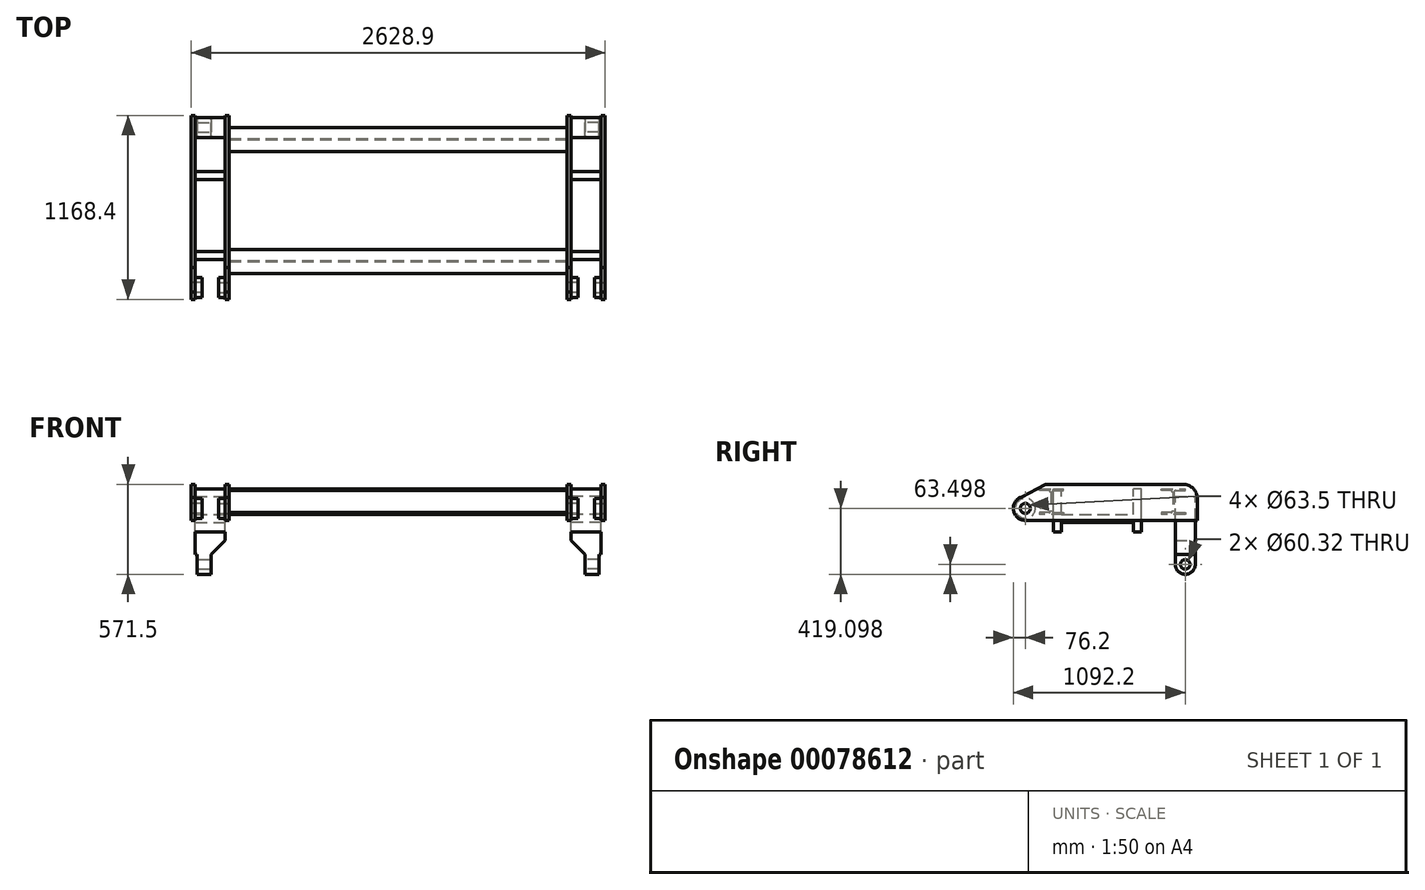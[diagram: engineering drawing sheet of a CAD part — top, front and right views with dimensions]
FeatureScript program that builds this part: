
annotation { "Feature Type Name" : "Feature", "Feature Type Description" : "" }
export const myFeature = defineFeature(function(context is Context, id is Id, definition is map)
    precondition{}
    {
        {
            var Q0;
            Q0=qCreatedBy(makeId("Right.planeOp"),FACE);
            var sketch = newSketch(context, id + "F0", { "sketchPlane" : qUnion([Q0])});
            skLineSegment(sketch, "E0", {"start": v(0, 94.66) * mm, "end": v(0, -108.5) * mm, "construction": true});
            skLineSegment(sketch, "E1.0", {"start": v(387.35, 94.66) * mm, "end": v(387.35, -76.51) * mm, "construction": true});
            skLineSegment(sketch, "E2", {"start": v(387.35, -6.92) * mm, "end": v(515.37, -6.92) * mm, "construction": true});
            skLineSegment(sketch, "E3.0", {"start": v(391.16, 49.98) * mm, "end": v(391.16, -63.81) * mm});
            skLineSegment(sketch, "E4.0", {"start": v(387.35, -87.94) * mm, "end": v(463.55, -87.94) * mm});
            skLineSegment(sketch, "E5.0", {"start": v(403.86, -76.51) * mm, "end": v(463.55, -76.51) * mm});
            skLineSegment(sketch, "E6.trimOffspring", {"start": v(463.55, -76.51) * mm, "end": v(463.55, -87.94) * mm});
            skLineSegment(sketch, "E7.0.MirrorCS", {"start": v(463.55, 62.68) * mm, "end": v(463.55, 74.11) * mm});
            skLineSegment(sketch, "E7.1.MirrorCS", {"start": v(387.35, 74.11) * mm, "end": v(463.55, 74.11) * mm});
            skLineSegment(sketch, "E7.2.MirrorCS", {"start": v(403.86, 62.68) * mm, "end": v(463.55, 62.68) * mm});
            skPoint(sketch, "E8.trimOffspring.end.orphan", {"position": v(387.35, -108.5) * mm});
            skLineSegment(sketch, "E9.0.MirrorCS", {"start": v(311.15, 62.68) * mm, "end": v(311.15, 74.11) * mm});
            skLineSegment(sketch, "E9.1.MirrorCS", {"start": v(311.15, -76.51) * mm, "end": v(311.15, -87.94) * mm});
            skLineSegment(sketch, "E9.2.MirrorCS", {"start": v(387.35, -87.94) * mm, "end": v(311.15, -87.94) * mm});
            skLineSegment(sketch, "E9.3.MirrorCS", {"start": v(383.54, 49.98) * mm, "end": v(383.54, -63.81) * mm});
            skLineSegment(sketch, "E9.4.MirrorCS", {"start": v(387.35, 74.11) * mm, "end": v(311.15, 74.11) * mm});
            skLineSegment(sketch, "E9.5.MirrorCS", {"start": v(370.84, 62.68) * mm, "end": v(311.15, 62.68) * mm});
            skLineSegment(sketch, "E9.6.MirrorCS", {"start": v(370.84, -76.51) * mm, "end": v(311.15, -76.51) * mm});
            skPoint(sketch, "E10.visualSharp", {"position": v(383.54, 62.68) * mm});
            skArc(sketch, "E10.filletArc", {"start": v(383.54, 49.98) * mm, "mid": v(379.82, 58.96) * mm, "end": v(370.84, 62.68) * mm});
            skPoint(sketch, "E11.visualSharp", {"position": v(391.16, 62.68) * mm});
            skArc(sketch, "E11.filletArc", {"start": v(403.86, 62.68) * mm, "mid": v(394.88, 58.96) * mm, "end": v(391.16, 49.98) * mm});
            skPoint(sketch, "E12.visualSharp", {"position": v(383.54, -76.51) * mm});
            skArc(sketch, "E12.filletArc", {"start": v(370.84, -76.51) * mm, "mid": v(379.82, -72.8) * mm, "end": v(383.54, -63.81) * mm});
            skPoint(sketch, "E13.visualSharp", {"position": v(391.16, -76.51) * mm});
            skArc(sketch, "E13.filletArc", {"start": v(391.16, -63.81) * mm, "mid": v(394.88, -72.8) * mm, "end": v(403.86, -76.51) * mm});
            skArc(sketch, "E14.0.MirrorCS", {"start": v(-403.86, 62.68) * mm, "mid": v(-394.88, 58.96) * mm, "end": v(-391.16, 49.98) * mm});
            skArc(sketch, "E14.1.MirrorCS", {"start": v(-391.16, -63.81) * mm, "mid": v(-394.88, -72.8) * mm, "end": v(-403.86, -76.51) * mm});
            skLineSegment(sketch, "E14.2.MirrorCS", {"start": v(-311.15, 62.68) * mm, "end": v(-311.15, 74.11) * mm});
            skArc(sketch, "E14.3.MirrorCS", {"start": v(-383.54, 49.98) * mm, "mid": v(-379.82, 58.96) * mm, "end": v(-370.84, 62.68) * mm});
            skArc(sketch, "E14.4.MirrorCS", {"start": v(-370.84, -76.51) * mm, "mid": v(-379.82, -72.8) * mm, "end": v(-383.54, -63.81) * mm});
            skLineSegment(sketch, "E14.5.MirrorCS", {"start": v(-311.15, -76.51) * mm, "end": v(-311.15, -87.94) * mm});
            skLineSegment(sketch, "E14.6.MirrorCS", {"start": v(-463.55, 62.68) * mm, "end": v(-463.55, 74.11) * mm});
            skLineSegment(sketch, "E14.7.MirrorCS", {"start": v(-463.55, -76.51) * mm, "end": v(-463.55, -87.94) * mm});
            skLineSegment(sketch, "E14.8.MirrorCS", {"start": v(-387.35, 94.66) * mm, "end": v(-387.35, -76.51) * mm, "construction": true});
            skPoint(sketch, "E14.9.MirrorP", {"position": v(-391.16, -76.51) * mm});
            skLineSegment(sketch, "E14.10.MirrorCS", {"start": v(-370.84, -76.51) * mm, "end": v(-311.15, -76.51) * mm});
            skPoint(sketch, "E14.11.MirrorP", {"position": v(-387.35, -108.5) * mm});
            skLineSegment(sketch, "E14.12.MirrorCS", {"start": v(-383.54, 49.98) * mm, "end": v(-383.54, -63.81) * mm});
            skPoint(sketch, "E14.13.MirrorP", {"position": v(-391.16, 62.68) * mm});
            skLineSegment(sketch, "E14.14.MirrorCS", {"start": v(-403.86, 62.68) * mm, "end": v(-463.55, 62.68) * mm});
            skLineSegment(sketch, "E14.15.MirrorCS", {"start": v(-403.86, -76.51) * mm, "end": v(-463.55, -76.51) * mm});
            skLineSegment(sketch, "E14.16.MirrorCS", {"start": v(-370.84, 62.68) * mm, "end": v(-311.15, 62.68) * mm});
            skLineSegment(sketch, "E14.17.MirrorCS", {"start": v(-387.35, 74.11) * mm, "end": v(-463.55, 74.11) * mm});
            skLineSegment(sketch, "E14.18.MirrorCS", {"start": v(-387.35, 74.11) * mm, "end": v(-311.15, 74.11) * mm});
            skPoint(sketch, "E14.19.MirrorP", {"position": v(-383.54, -76.51) * mm});
            skLineSegment(sketch, "E14.20.MirrorCS", {"start": v(-387.35, -87.94) * mm, "end": v(-463.55, -87.94) * mm});
            skPoint(sketch, "E14.21.MirrorP", {"position": v(-383.54, 62.68) * mm});
            skLineSegment(sketch, "E14.22.MirrorCS", {"start": v(-387.35, -87.94) * mm, "end": v(-311.15, -87.94) * mm});
            skLineSegment(sketch, "E14.23.MirrorCS", {"start": v(-391.16, 49.98) * mm, "end": v(-391.16, -63.81) * mm});
            skSolve(sketch);
        }
        {
            var Q0;
            Q0=qSketchRegion(id+"F0",true);
            extrude(context, id + "F1", {"entities" : qUnion([Q0]), "endBound" : BoundingType.SYMMETRIC, "depth" : 2146.3 * mm});
        }
        {
            var Q0;
            Q0=makeQuery(id+"F1.opExtrude","CAP_FACE",FACE,{"disambiguationData":[OSD([sQuery(id+"F0.wireOp",EDGE,"E14.0.MirrorCS"),sQuery(id+"F0.wireOp",EDGE,"E14.1.MirrorCS"),sQuery(id+"F0.wireOp",EDGE,"E14.2.MirrorCS"),sQuery(id+"F0.wireOp",EDGE,"E14.3.MirrorCS"),sQuery(id+"F0.wireOp",EDGE,"E14.4.MirrorCS"),sQuery(id+"F0.wireOp",EDGE,"E14.5.MirrorCS"),sQuery(id+"F0.wireOp",EDGE,"E14.6.MirrorCS"),sQuery(id+"F0.wireOp",EDGE,"E14.7.MirrorCS"),sQuery(id+"F0.wireOp",EDGE,"E14.10.MirrorCS"),sQuery(id+"F0.wireOp",EDGE,"E14.12.MirrorCS"),sQuery(id+"F0.wireOp",EDGE,"E14.14.MirrorCS"),sQuery(id+"F0.wireOp",EDGE,"E14.15.MirrorCS"),sQuery(id+"F0.wireOp",EDGE,"E14.16.MirrorCS"),sQuery(id+"F0.wireOp",EDGE,"E14.17.MirrorCS"),sQuery(id+"F0.wireOp",EDGE,"E14.18.MirrorCS"),sQuery(id+"F0.wireOp",EDGE,"E14.20.MirrorCS"),sQuery(id+"F0.wireOp",EDGE,"E14.22.MirrorCS"),sQuery(id+"F0.wireOp",EDGE,"E14.23.MirrorCS")])],"isStart":false});
            var sketch = newSketch(context, id + "F2", { "sketchPlane" : qUnion([Q0])});
            skLineSegment(sketch, "E15.0", {"start": v(311.15, 74.11) * mm, "end": v(463.55, 74.11) * mm, "construction": true});
            skLineSegment(sketch, "E16", {"start": v(387.35, 74.11) * mm, "end": v(387.35, -187.68) * mm, "construction": true});
            skLineSegment(sketch, "E17", {"start": v(539.75, 13.66) * mm, "end": v(539.75, -126.04) * mm});
            skLineSegment(sketch, "E18.0", {"start": v(450.85, 102.56) * mm, "end": v(-425.45, 102.56) * mm});
            skPoint(sketch, "E19.visualSharp", {"position": v(539.75, 102.56) * mm});
            skArc(sketch, "E19.filletArc", {"start": v(539.75, 13.66) * mm, "mid": v(513.71, 76.52) * mm, "end": v(450.85, 102.56) * mm});
            skLineSegment(sketch, "E20.0", {"start": v(-628.65, 13.66) * mm, "end": v(-628.65, -213.35) * mm});
            skLineSegment(sketch, "E21.0", {"start": v(-552.45, -49.84) * mm, "end": v(-552.45, -126.04) * mm});
            skLineSegment(sketch, "E22", {"start": v(-424, -87.94) * mm, "end": v(-671.77, -87.94) * mm, "construction": true});
            skLineSegment(sketch, "E23.0", {"start": v(-424, -49.84) * mm, "end": v(-425.45, -49.84) * mm});
            skArc(sketch, "E24", {"start": v(-580.33, 21.07) * mm, "mid": v(-627.32, -64.03) * mm, "end": v(-552.45, -126.04) * mm});
            skLineSegment(sketch, "E25", {"start": v(-425.45, 102.56) * mm, "end": v(-595.1, 13.3) * mm});
            skLineSegment(sketch, "E26", {"start": v(-552.45, -126.04) * mm, "end": v(539.75, -126.04) * mm});
            skLineSegment(sketch, "E27.trimOffspring", {"start": v(-628.65, -49.84) * mm, "end": v(-671.77, -49.84) * mm});
            skCircle(sketch, "E28", {"center": v(-552.45, -49.84) * mm, "radius": 31.75 * mm});
            skSolve(sketch);
        }
        {
            var Q0;
            Q0=qSketchRegion(id+"F2",true);
            extrude(context, id + "F3", {"entities" : qUnion([Q0]), "depth" : 25.4 * mm});
        }
        {
            var Q0;
            Q0=makeQuery(id+"F3.opExtrude","CAP_FACE",FACE,{"disambiguationData":[OSD([sQuery(id+"F2.wireOp",EDGE,"E17"),sQuery(id+"F2.wireOp",EDGE,"E18.0"),sQuery(id+"F2.wireOp",EDGE,"E19.filletArc"),sQuery(id+"F2.wireOp",EDGE,"E24"),sQuery(id+"F2.wireOp",EDGE,"E25"),sQuery(id+"F2.wireOp",EDGE,"E26"),sQuery(id+"F2.wireOp",EDGE,"E28")])],"isStart":false});
            var sketch = newSketch(context, id + "F4", { "sketchPlane" : qUnion([Q0])});
            skCircle(sketch, "E29", {"center": v(-552.45, -49.84) * mm, "radius": 63.5 * mm});
            skCircle(sketch, "E30.0", {"center": v(-552.45, -49.84) * mm, "radius": 31.75 * mm});
            skSolve(sketch);
        }
        {
            var Q0;
            Q0=qSketchRegion(id+"F4",true);
            extrude(context, id + "F5", {"entities" : qUnion([Q0]), "operationType" : NewBodyOperationType.ADD, "depth" : 43.69 * mm});
        }
        {
            var Q0;
            Q0=makeQuery(id+"F3.opExtrude","CAP_FACE",FACE,{"disambiguationData":[OSD([sQuery(id+"F2.wireOp",EDGE,"E17"),sQuery(id+"F2.wireOp",EDGE,"E18.0"),sQuery(id+"F2.wireOp",EDGE,"E19.filletArc"),sQuery(id+"F2.wireOp",EDGE,"E24"),sQuery(id+"F2.wireOp",EDGE,"E25"),sQuery(id+"F2.wireOp",EDGE,"E26"),sQuery(id+"F2.wireOp",EDGE,"E28")])],"isStart":false});
            var sketch = newSketch(context, id + "F6", { "sketchPlane" : qUnion([Q0])});
            skLineSegment(sketch, "E31.0", {"start": v(311.15, 74.11) * mm, "end": v(463.55, 74.11) * mm, "construction": true});
            skLineSegment(sketch, "E32", {"start": v(387.35, 74.11) * mm, "end": v(387.35, 301) * mm, "construction": true});
            skLineSegment(sketch, "E33", {"start": v(184.15, 74.11) * mm, "end": v(133.35, 74.11) * mm});
            skLineSegment(sketch, "E34", {"start": v(463.55, 74.11) * mm, "end": v(463.55, 349.58) * mm, "construction": true});
            skLineSegment(sketch, "E35.0", {"start": v(-95.25, 74.11) * mm, "end": v(-95.25, 349.58) * mm, "construction": true});
            skLineSegment(sketch, "E36.0", {"start": v(133.35, -198.94) * mm, "end": v(133.35, -138.74) * mm});
            skLineSegment(sketch, "E37.0", {"start": v(184.15, -198.94) * mm, "end": v(184.15, 74.11) * mm});
            skLineSegment(sketch, "E38.0", {"start": v(184.15, -198.94) * mm, "end": v(133.35, -198.94) * mm});
            skLineSegment(sketch, "E39", {"start": v(-552.45, -49.84) * mm, "end": v(714.62, -49.84) * mm, "construction": true});
            skLineSegment(sketch, "E40.0", {"start": v(-323.85, -138.74) * mm, "end": v(133.35, -138.74) * mm});
            skLineSegment(sketch, "E41.0", {"start": v(-323.85, -87.94) * mm, "end": v(133.35, -87.94) * mm});
            skLineSegment(sketch, "E42.0.MirrorCS", {"start": v(-323.85, -198.94) * mm, "end": v(-323.85, -138.74) * mm});
            skLineSegment(sketch, "E42.1.MirrorCS", {"start": v(-374.65, -198.94) * mm, "end": v(-374.65, 74.11) * mm});
            skLineSegment(sketch, "E42.2.MirrorCS", {"start": v(-374.65, 74.11) * mm, "end": v(-323.85, 74.11) * mm});
            skLineSegment(sketch, "E42.3.MirrorCS", {"start": v(-374.65, -198.94) * mm, "end": v(-323.85, -198.94) * mm});
            skLineSegment(sketch, "E43.trimOffspring", {"start": v(-323.85, -87.94) * mm, "end": v(-323.85, 74.11) * mm});
            skLineSegment(sketch, "E44.trimOffspring", {"start": v(133.35, -87.94) * mm, "end": v(133.35, 74.11) * mm});
            skSolve(sketch);
        }
        {
            var Q0;
            Q0=qSketchRegion(id+"F6",true);
            extrude(context, id + "F7", {"entities" : qUnion([Q0]), "depth" : 190.5 * mm});
        }
        {
            var Q0;
            Q0=makeQuery(id+"F3.opExtrude","CAP_FACE",FACE,{"disambiguationData":[OSD([sQuery(id+"F2.wireOp",EDGE,"E17"),sQuery(id+"F2.wireOp",EDGE,"E18.0"),sQuery(id+"F2.wireOp",EDGE,"E19.filletArc"),sQuery(id+"F2.wireOp",EDGE,"E24"),sQuery(id+"F2.wireOp",EDGE,"E25"),sQuery(id+"F2.wireOp",EDGE,"E26"),sQuery(id+"F2.wireOp",EDGE,"E28")])],"isStart":false});
            cPlane(context, id + "F8", {"entities" : qUnion([Q0]), "cplaneType" : CPlaneType.OFFSET, "offset" : 95.25 * mm, "width" : 152.4 * mm, "height" : 152.4 * mm});
        }
        {
            var Q0;
            Q0=makeQuery(id+"F3.opExtrude","SWEPT_BODY",BODY,{"disambiguationData":[OSD([sQuery(id+"F2.wireOp",EDGE,"E17"),sQuery(id+"F2.wireOp",EDGE,"E18.0"),sQuery(id+"F2.wireOp",EDGE,"E19.filletArc"),sQuery(id+"F2.wireOp",EDGE,"E24"),sQuery(id+"F2.wireOp",EDGE,"E25"),sQuery(id+"F2.wireOp",EDGE,"E26"),sQuery(id+"F2.wireOp",EDGE,"E28")])]});
            var Q1;
            Q1=qCreatedBy(id+"F8.planeOp",FACE);
            mirror(context, id + "F9", {"entities" : qUnion([Q0]), "mirrorPlane" : qUnion([Q1])});
        }
        {
            var Q0;
            Q0=makeQuery(id+"F3.opExtrude","CAP_FACE",FACE,{"disambiguationData":[OSD([sQuery(id+"F2.wireOp",EDGE,"E17"),sQuery(id+"F2.wireOp",EDGE,"E18.0"),sQuery(id+"F2.wireOp",EDGE,"E19.filletArc"),sQuery(id+"F2.wireOp",EDGE,"E24"),sQuery(id+"F2.wireOp",EDGE,"E25"),sQuery(id+"F2.wireOp",EDGE,"E26"),sQuery(id+"F2.wireOp",EDGE,"E28")])],"isStart":false});
            var sketch = newSketch(context, id + "F10", { "sketchPlane" : qUnion([Q0])});
            skLineSegment(sketch, "E45.0", {"start": v(-323.85, -138.74) * mm, "end": v(133.35, -138.74) * mm, "construction": true});
            skLineSegment(sketch, "E46", {"start": v(-95.25, -138.74) * mm, "end": v(-95.25, -453.43) * mm, "construction": true});
            skLineSegment(sketch, "E47", {"start": v(-552.45, -49.84) * mm, "end": v(812.78, -49.84) * mm, "construction": true});
            skArc(sketch, "E48", {"start": v(400.05, -405.44) * mm, "mid": v(463.55, -468.94) * mm, "end": v(527.05, -405.44) * mm});
            skLineSegment(sketch, "E49.0", {"start": v(400.05, 26.36) * mm, "end": v(527.05, 26.36) * mm});
            skLineSegment(sketch, "E50", {"start": v(527.05, -405.44) * mm, "end": v(527.05, 26.36) * mm});
            skLineSegment(sketch, "E51", {"start": v(400.05, -405.44) * mm, "end": v(400.05, 26.36) * mm});
            skCircle(sketch, "E52", {"center": v(463.55, -405.44) * mm, "radius": 30.16 * mm});
            skSolve(sketch);
        }
        {
            var Q0;
            Q0=qSketchRegion(id+"F10",true);
            extrude(context, id + "F11", {"entities" : qUnion([Q0]), "operationType" : NewBodyOperationType.ADD, "depth" : 190.5 * mm});
        }
        {
            var Q0;
            Q0=makeQuery(id+"F11.opExtrude","SWEPT_FACE",FACE,{"disambiguationData":[OSD([sQuery(id+"F10.wireOp",EDGE,"E50")])]});
            var sketch = newSketch(context, id + "F12", { "sketchPlane" : qUnion([Q0])});
            skLineSegment(sketch, "E53", {"start": v(0, 0) * mm, "end": v(0, -692.7) * mm, "construction": true});
            skLineSegment(sketch, "E54", {"start": v(-1098.55, -468.94) * mm, "end": v(-1289.05, -468.94) * mm, "construction": true});
            skLineSegment(sketch, "E55.0", {"start": v(-1098.55, -341.94) * mm, "end": v(-1289.05, -341.94) * mm, "construction": true});
            skLineSegment(sketch, "E56.0", {"start": v(1187.45, 0) * mm, "end": v(1187.45, -692.7) * mm, "construction": true});
            skLineSegment(sketch, "E57.0.MirrorCS", {"start": v(-1187.45, 0) * mm, "end": v(-1187.45, -692.7) * mm, "construction": true});
            skLineSegment(sketch, "E58.0", {"start": v(-1276.35, 0) * mm, "end": v(-1276.35, -692.7) * mm, "construction": true});
            skLineSegment(sketch, "E59.bottom", {"start": v(-1289.05, -468.94) * mm, "end": v(-1276.35, -468.94) * mm});
            skLineSegment(sketch, "E59.top", {"start": v(-1289.05, -341.94) * mm, "end": v(-1276.35, -341.94) * mm});
            skLineSegment(sketch, "E59.left", {"start": v(-1289.05, -468.94) * mm, "end": v(-1289.05, -341.94) * mm});
            skLineSegment(sketch, "E59.right", {"start": v(-1276.35, -468.94) * mm, "end": v(-1276.35, -341.94) * mm});
            skLineSegment(sketch, "E60", {"start": v(-1187.45, -468.94) * mm, "end": v(-1187.45, -341.94) * mm});
            skLineSegment(sketch, "E61", {"start": v(-1187.45, -341.94) * mm, "end": v(-1032.6, -187.1) * mm});
            skLineSegment(sketch, "E62", {"start": v(-1032.6, -187.1) * mm, "end": v(-1032.6, -590.93) * mm});
            skLineSegment(sketch, "E63", {"start": v(-1032.6, -590.93) * mm, "end": v(-1187.45, -590.93) * mm});
            skLineSegment(sketch, "E64", {"start": v(-1187.45, -590.93) * mm, "end": v(-1187.45, -468.94) * mm});
            skSolve(sketch);
        }
        {
            var Q0;
            Q0=qSketchRegion(id+"F12",true);
            extrude(context, id + "F13", {"entities" : qUnion([Q0]), "operationType" : NewBodyOperationType.REMOVE, "endBound" : BoundingType.THROUGH_ALL, "oppositeDirection" : true, "depth" : 25.4 * mm});
        }
        {
            var Q0;
            Q0=makeQuery(id+"F3.opExtrude","SWEPT_BODY",BODY,{"disambiguationData":[OSD([sQuery(id+"F2.wireOp",EDGE,"E17"),sQuery(id+"F2.wireOp",EDGE,"E18.0"),sQuery(id+"F2.wireOp",EDGE,"E19.filletArc"),sQuery(id+"F2.wireOp",EDGE,"E24"),sQuery(id+"F2.wireOp",EDGE,"E25"),sQuery(id+"F2.wireOp",EDGE,"E26"),sQuery(id+"F2.wireOp",EDGE,"E28")])]});
            var Q1;
            Q1=makeQuery(id+"F7.opExtrude","SWEPT_BODY",BODY,{"disambiguationData":[OSD([sQuery(id+"F6.wireOp",EDGE,"E33"),sQuery(id+"F6.wireOp",EDGE,"E36.0"),sQuery(id+"F6.wireOp",EDGE,"E37.0"),sQuery(id+"F6.wireOp",EDGE,"E38.0"),sQuery(id+"F6.wireOp",EDGE,"E40.0"),sQuery(id+"F6.wireOp",EDGE,"E41.0"),sQuery(id+"F6.wireOp",EDGE,"E42.0.MirrorCS"),sQuery(id+"F6.wireOp",EDGE,"E42.1.MirrorCS"),sQuery(id+"F6.wireOp",EDGE,"E42.2.MirrorCS"),sQuery(id+"F6.wireOp",EDGE,"E42.3.MirrorCS"),sQuery(id+"F6.wireOp",EDGE,"E43.trimOffspring"),sQuery(id+"F6.wireOp",EDGE,"E44.trimOffspring")])]});
            var Q2;
            Q2=makeQuery(id+"F9.opPattern","COPY",BODY,{"derivedFrom":makeQuery(id+"F3.opExtrude","SWEPT_BODY",BODY,{"disambiguationData":[OSD([sQuery(id+"F2.wireOp",EDGE,"E17"),sQuery(id+"F2.wireOp",EDGE,"E18.0"),sQuery(id+"F2.wireOp",EDGE,"E19.filletArc"),sQuery(id+"F2.wireOp",EDGE,"E24"),sQuery(id+"F2.wireOp",EDGE,"E25"),sQuery(id+"F2.wireOp",EDGE,"E26"),sQuery(id+"F2.wireOp",EDGE,"E28")])]}),"instanceName":"1"});
            var Q3;
            Q3=qCreatedBy(makeId("Right.planeOp"),FACE);
            mirror(context, id + "F14", {"entities" : qUnion([Q0, Q1, Q2]), "mirrorPlane" : qUnion([Q3])});
        }
    });
